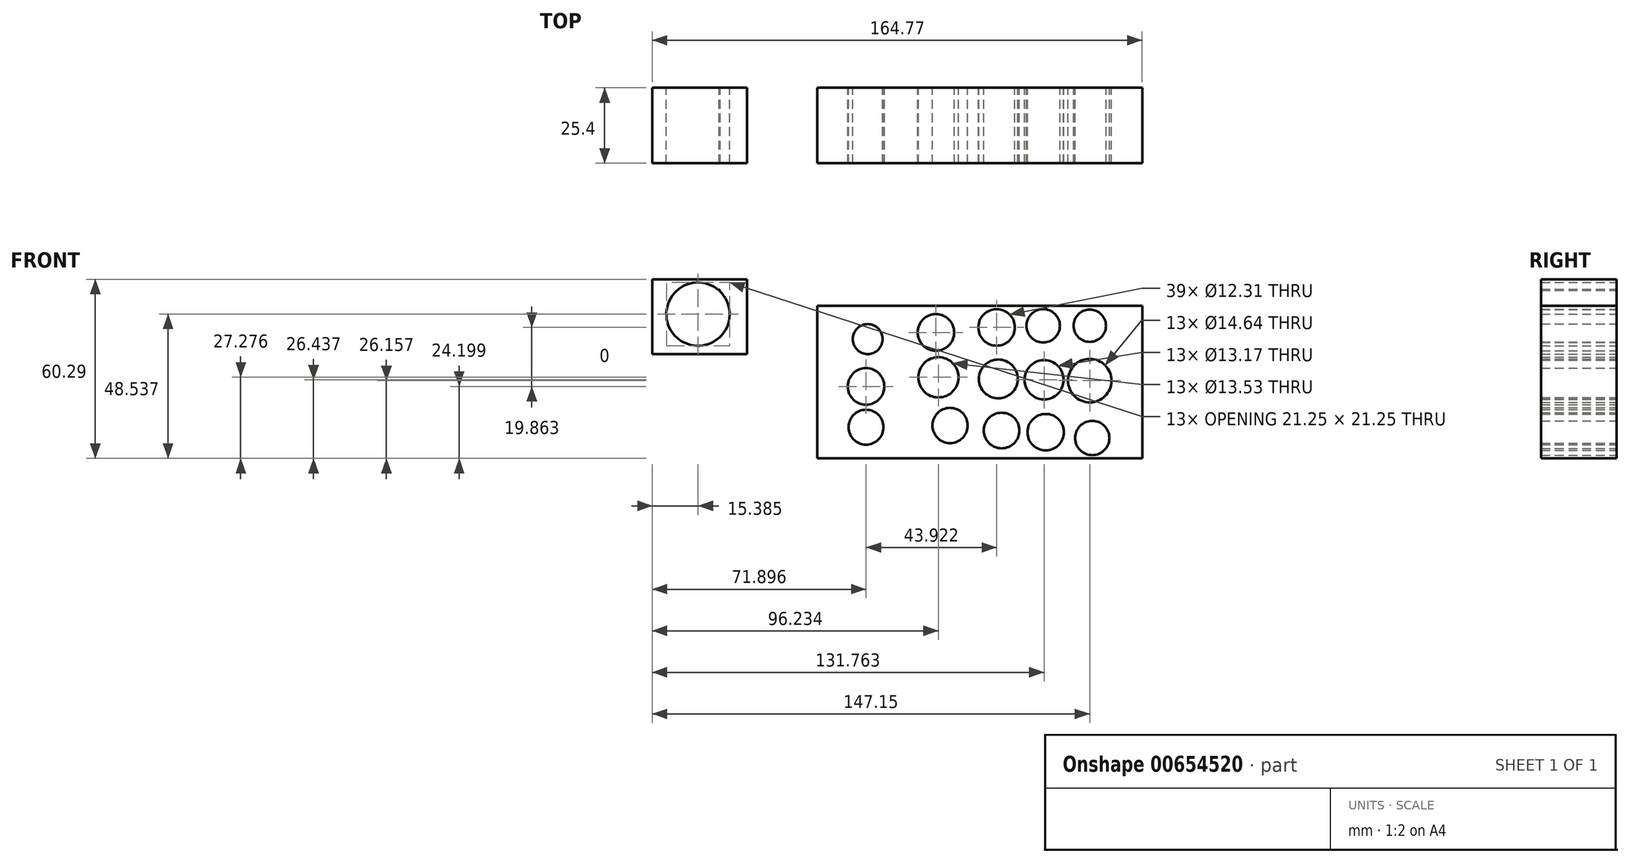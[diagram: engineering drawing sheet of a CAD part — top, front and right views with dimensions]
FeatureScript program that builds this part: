
annotation { "Feature Type Name" : "Feature", "Feature Type Description" : "" }
export const myFeature = defineFeature(function(context is Context, id is Id, definition is map)
    precondition{}
    {
        {
            var Q0;
            Q0=qCreatedBy(makeId("Front.planeOp"),FACE);
            var sketch = newSketch(context, id + "F0", { "sketchPlane" : qUnion([Q0])});
            skLineSegment(sketch, "E0", {"start": v(-55.53, 60.29) * mm, "end": v(-23.64, 60.29) * mm});
            skLineSegment(sketch, "E1", {"start": v(-23.64, 60.29) * mm, "end": v(-23.64, 35.1) * mm});
            skLineSegment(sketch, "E2", {"start": v(-23.64, 35.1) * mm, "end": v(-55.53, 35.1) * mm});
            skLineSegment(sketch, "E3", {"start": v(-55.53, 35.1) * mm, "end": v(-55.53, 60.29) * mm});
            skCircle(sketch, "E4", {"center": v(-40.14, 48.54) * mm, "radius": 10.65 * mm});
            skLineSegment(sketch, "E5", {"start": v(-40.14, 48.54) * mm, "end": v(-40.14, 59.18) * mm});
            skLineSegment(sketch, "E6", {"start": v(-40.14, 59.18) * mm, "end": v(-40.14, 37.9) * mm});
            skLineSegment(sketch, "E7", {"start": v(-40.14, 37.9) * mm, "end": v(-40.14, 48.54) * mm});
            skLineSegment(sketch, "E8", {"start": v(-29.5, 48.54) * mm, "end": v(-40.14, 48.54) * mm});
            skLineSegment(sketch, "E9", {"start": v(-50.8, 48.54) * mm, "end": v(-40.14, 48.54) * mm});
            skLineSegment(sketch, "E10", {"start": v(-40.14, 48.54) * mm, "end": v(-48.1, 55.62) * mm});
            skLineSegment(sketch, "E11", {"start": v(-48.1, 55.62) * mm, "end": v(-32.63, 41) * mm});
            skLineSegment(sketch, "E12", {"start": v(-32.63, 41) * mm, "end": v(-40.14, 48.54) * mm});
            skLineSegment(sketch, "E13", {"start": v(-40.14, 48.54) * mm, "end": v(-32.63, 56.98) * mm});
            skLineSegment(sketch, "E14", {"start": v(-32.63, 56.98) * mm, "end": v(-47.66, 41) * mm});
            skLineSegment(sketch, "E15", {"start": v(-47.66, 41) * mm, "end": v(-32.63, 56.98) * mm});
            skLineSegment(sketch, "E16", {"start": v(0, 0) * mm, "end": v(0, 51.34) * mm});
            skLineSegment(sketch, "E17", {"start": v(0, 51.34) * mm, "end": v(109.24, 51.34) * mm});
            skLineSegment(sketch, "E18", {"start": v(109.24, 51.34) * mm, "end": v(109.24, 0) * mm});
            skLineSegment(sketch, "E19", {"start": v(109.24, 0) * mm, "end": v(0, 0) * mm});
            skCircle(sketch, "E20", {"center": v(16.93, 40.14) * mm, "radius": 5.04 * mm});
            skCircle(sketch, "E21", {"center": v(16.37, 24.2) * mm, "radius": 6.15 * mm});
            skCircle(sketch, "E22", {"center": v(16.37, 10.5) * mm, "radius": 5.87 * mm});
            skCircle(sketch, "E23", {"center": v(44.62, 11.05) * mm, "radius": 5.93 * mm});
            skCircle(sketch, "E24", {"center": v(40.7, 27.28) * mm, "radius": 6.77 * mm});
            skCircle(sketch, "E25", {"center": v(39.87, 42.38) * mm, "radius": 6.15 * mm});
            skCircle(sketch, "E26", {"center": v(60.29, 44.06) * mm, "radius": 6.15 * mm});
            skCircle(sketch, "E27", {"center": v(60.85, 26.72) * mm, "radius": 6.53 * mm});
            skCircle(sketch, "E28", {"center": v(61.97, 9.37) * mm, "radius": 5.98 * mm});
            skCircle(sketch, "E29", {"center": v(76.8, 8.81) * mm, "radius": 6.14 * mm});
            skCircle(sketch, "E30", {"center": v(76.23, 26.44) * mm, "radius": 6.58 * mm});
            skCircle(sketch, "E31", {"center": v(75.95, 44.62) * mm, "radius": 5.62 * mm});
            skCircle(sketch, "E32", {"center": v(91.62, 44.62) * mm, "radius": 5.43 * mm});
            skCircle(sketch, "E33", {"center": v(91.62, 26.16) * mm, "radius": 7.32 * mm});
            skCircle(sketch, "E34", {"center": v(92.46, 6.85) * mm, "radius": 5.77 * mm});
            skCircle(sketch, "E35", {"center": v(16.93, 40.14) * mm, "radius": 3.64 * mm});
            skCircle(sketch, "E36", {"center": v(16.37, 24.2) * mm, "radius": 3.96 * mm});
            skCircle(sketch, "E37", {"center": v(16.37, 10.5) * mm, "radius": 3.8 * mm});
            skCircle(sketch, "E38", {"center": v(40.7, 27.28) * mm, "radius": 4.89 * mm});
            skCircle(sketch, "E39", {"center": v(39.87, 42.38) * mm, "radius": 3.96 * mm});
            skCircle(sketch, "E40", {"center": v(44.62, 11.05) * mm, "radius": 4.48 * mm});
            skCircle(sketch, "E41", {"center": v(61.97, 9.37) * mm, "radius": 4.2 * mm});
            skCircle(sketch, "E42", {"center": v(60.85, 26.72) * mm, "radius": 4.34 * mm});
            skCircle(sketch, "E43", {"center": v(60.29, 44.06) * mm, "radius": 4.23 * mm});
            skCircle(sketch, "E44", {"center": v(75.95, 44.62) * mm, "radius": 3.75 * mm});
            skCircle(sketch, "E45", {"center": v(76.23, 26.44) * mm, "radius": 4.48 * mm});
            skCircle(sketch, "E46", {"center": v(76.8, 8.81) * mm, "radius": 3.8 * mm});
            skCircle(sketch, "E47", {"center": v(92.46, 6.85) * mm, "radius": 4.34 * mm});
            skCircle(sketch, "E48", {"center": v(91.62, 26.16) * mm, "radius": 5.07 * mm});
            skCircle(sketch, "E49", {"center": v(91.62, 44.62) * mm, "radius": 3.8 * mm});
            skSolve(sketch);
        }
        {
            var Q0;
            Q0 = qSketchRegion(id + "F0", true);
            extrude(context, id + "F1", {"entities" : qUnion([Q0]), "depth" : 25.4 * mm, "offsetDistance" : 25.4 * mm});
        }
    });
